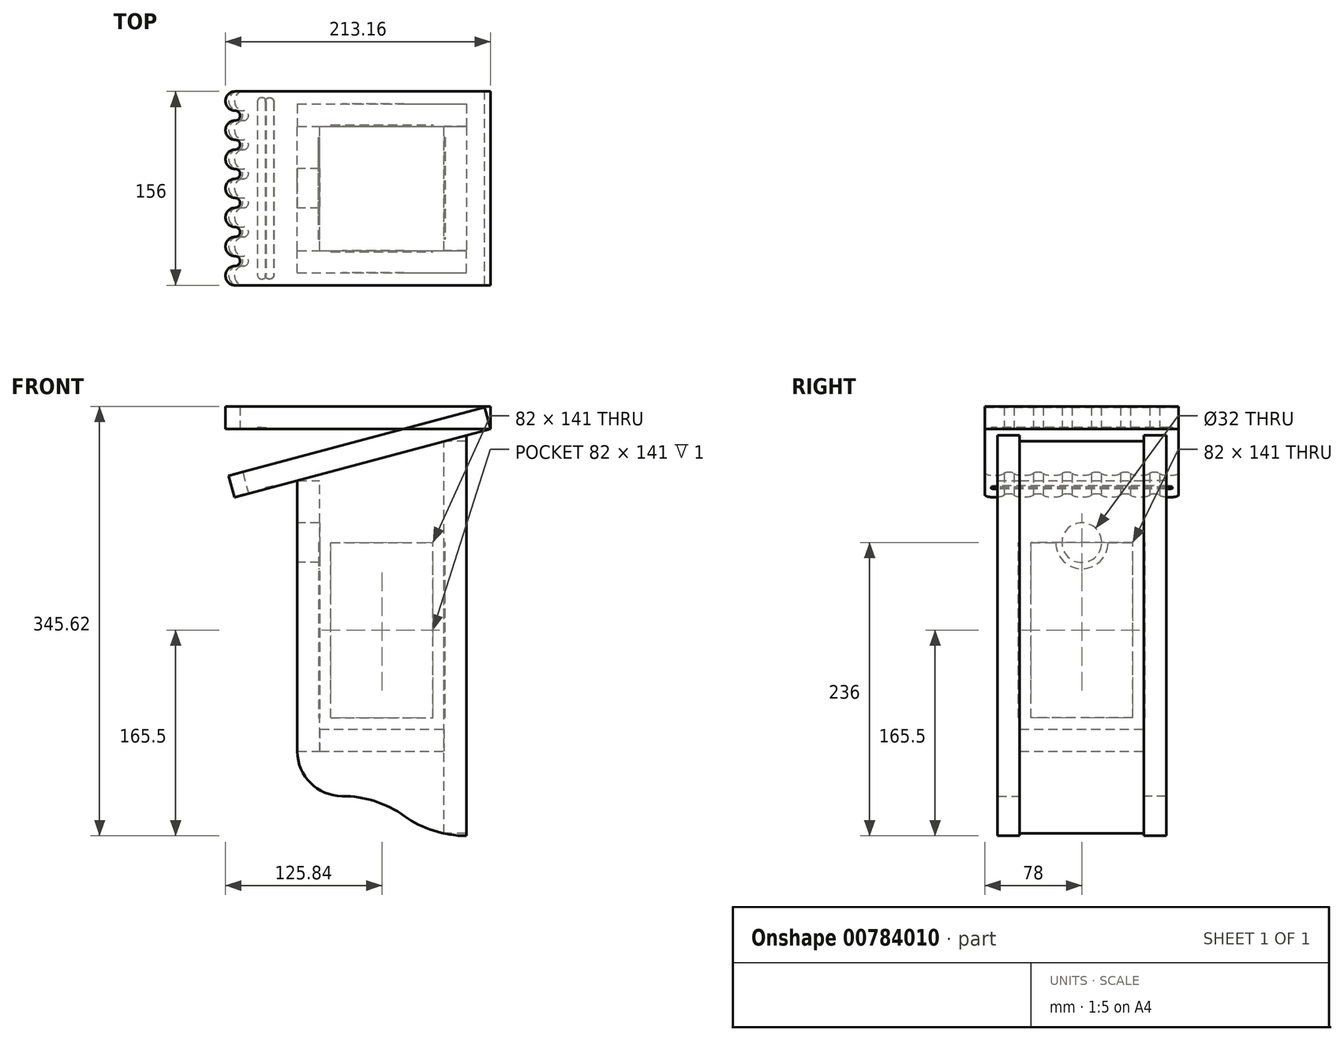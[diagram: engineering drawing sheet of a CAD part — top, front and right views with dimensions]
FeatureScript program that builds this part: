
annotation { "Feature Type Name" : "Feature", "Feature Type Description" : "" }
export const myFeature = defineFeature(function(context is Context, id is Id, definition is map)
    precondition{}
    {
        {
            assignVariable(context, id + "F0", {"name" : "Larg", "anyValue" : 100});
        }
        {
            assignVariable(context, id + "F1", {"name" : "Ep", "anyValue" : 18});
        }
        {
            var Q0;
            Q0=qCreatedBy(makeId("Front.planeOp"),FACE);
            cPlane(context, id + "F2", {"entities" : qUnion([Q0]), "cplaneType" : CPlaneType.OFFSET, "offset" : (getVariable(context, 'Larg') / 2) * mm, "width" : 150 * mm, "height" : 150 * mm});
        }
        {
            var Q0;
            Q0=qCreatedBy(id+"F2.planeOp",FACE);
            var sketch = newSketch(context, id + "F3", { "sketchPlane" : qUnion([Q0])});
            skLineSegment(sketch, "E0", {"start": v(-68, -109) * mm, "end": v(-68, 109) * mm});
            skLineSegment(sketch, "E1", {"start": v(-68, 109) * mm, "end": v(68, 145.44) * mm});
            skLineSegment(sketch, "E2", {"start": v(68, 145.44) * mm, "end": v(68, -109) * mm});
            skLineSegment(sketch, "E3", {"start": v(68, -109) * mm, "end": v(-68, -109) * mm});
            skLineSegment(sketch, "E4", {"start": v(68, -109) * mm, "end": v(68, -177) * mm});
            skArc(sketch, "E5", {"start": v(-68, -109) * mm, "mid": v(-57.46, -134.46) * mm, "end": v(-32, -145) * mm});
            skArc(sketch, "E6", {"start": v(-32, -145) * mm, "mid": v(-5.75, -149.1) * mm, "end": v(18, -161) * mm});
            skArc(sketch, "E7", {"start": v(68, -177) * mm, "mid": v(41.75, -172.9) * mm, "end": v(18, -161) * mm});
            skSolve(sketch);
        }
        {
            var Q0;
            Q0=qSketchRegion(id+"F3",true);
            extrude(context, id + "F4", {"entities" : qUnion([Q0]), "depth" : (getVariable(context, 'Ep')) * mm, "offsetDistance" : 25 * mm});
        }
        {
            var Q0;
            Q0=makeQuery(id+"F4.opExtrude","CAP_FACE",FACE,{"disambiguationData":[OSD([sQuery(id+"F3.wireOp",EDGE,"E0"),sQuery(id+"F3.wireOp",EDGE,"E1"),sQuery(id+"F3.wireOp",EDGE,"E2"),sQuery(id+"F3.wireOp",EDGE,"E4"),sQuery(id+"F3.wireOp",EDGE,"E5"),sQuery(id+"F3.wireOp",EDGE,"E6"),sQuery(id+"F3.wireOp",EDGE,"E7")])],"isStart":true});
            var sketch = newSketch(context, id + "F5", { "sketchPlane" : qUnion([Q0])});
            skLineSegment(sketch, "E8.bottom", {"start": v(41, -82) * mm, "end": v(-41, -82) * mm});
            skLineSegment(sketch, "E8.top", {"start": v(41, 59) * mm, "end": v(-41, 59) * mm});
            skLineSegment(sketch, "E8.left", {"start": v(41, -82) * mm, "end": v(41, 59) * mm});
            skLineSegment(sketch, "E8.right", {"start": v(-41, -82) * mm, "end": v(-41, 59) * mm});
            skSolve(sketch);
        }
        {
            var Q0;
            Q0 = qSketchRegion(id + "F5", true);
            extrude(context, id + "F6", {"entities" : qUnion([Q0]), "operationType" : NewBodyOperationType.REMOVE, "oppositeDirection" : true, "depth" : 1 * mm, "offsetDistance" : 25 * mm});
        }
        {
            var Q0;
            Q0=makeQuery(id+"F4.opExtrude","SWEPT_BODY",BODY,{"disambiguationData":[OSD([sQuery(id+"F3.wireOp",EDGE,"z3EwWfGW-5xOQ-D7vt-vxF3-r7Dkdny4VjHE"),sQuery(id+"F3.wireOp",EDGE,"Gt7UUSWQ-Rokf-2xSb-CDKS-a55I8TqbTzyF"),sQuery(id+"F3.wireOp",EDGE,"E0"),sQuery(id+"F3.wireOp",EDGE,"E1"),sQuery(id+"F3.wireOp",EDGE,"E2"),sQuery(id+"F3.wireOp",EDGE,"E3")])]});
            var Q1;
            Q1=qCreatedBy(makeId("Front.planeOp"),FACE);
            mirror(context, id + "F7", {"entities" : qUnion([Q0]), "mirrorPlane" : qUnion([Q1])});
        }
        {
            var Q0;
            Q0=makeQuery(id+"F7.opPattern","COPY",FACE,{"derivedFrom":makeQuery(id+"F4.opExtrude","CAP_FACE",FACE,{"disambiguationData":[OSD([sQuery(id+"F3.wireOp",EDGE,"z3EwWfGW-5xOQ-D7vt-vxF3-r7Dkdny4VjHE"),sQuery(id+"F3.wireOp",EDGE,"Gt7UUSWQ-Rokf-2xSb-CDKS-a55I8TqbTzyF"),sQuery(id+"F3.wireOp",EDGE,"E0"),sQuery(id+"F3.wireOp",EDGE,"E1"),sQuery(id+"F3.wireOp",EDGE,"E2"),sQuery(id+"F3.wireOp",EDGE,"E3")])],"isStart":true}),"instanceName":"1"});
            var sketch = newSketch(context, id + "F8", { "sketchPlane" : qUnion([Q0])});
            skLineSegment(sketch, "E9.bottom", {"start": v(-68, -109) * mm, "end": v(-50, -109) * mm});
            skLineSegment(sketch, "E9.top", {"start": v(-68, 109) * mm, "end": v(-50, 109) * mm});
            skLineSegment(sketch, "E9.left", {"start": v(-68, -109) * mm, "end": v(-68, 109) * mm});
            skLineSegment(sketch, "E9.right", {"start": v(-50, -109) * mm, "end": v(-50, 109) * mm});
            skSolve(sketch);
        }
        {
            var Q0;
            Q0=qSketchRegion(id+"F8",true);
            var Q1;
            Q1=makeQuery(id+"F4.opExtrude","CAP_FACE",FACE,{"disambiguationData":[OSD([sQuery(id+"F3.wireOp",EDGE,"z3EwWfGW-5xOQ-D7vt-vxF3-r7Dkdny4VjHE"),sQuery(id+"F3.wireOp",EDGE,"Gt7UUSWQ-Rokf-2xSb-CDKS-a55I8TqbTzyF"),sQuery(id+"F3.wireOp",EDGE,"E0"),sQuery(id+"F3.wireOp",EDGE,"E1"),sQuery(id+"F3.wireOp",EDGE,"E2"),sQuery(id+"F3.wireOp",EDGE,"E3")])],"isStart":true});
            extrude(context, id + "F9", {"entities" : qUnion([Q0]), "endBound" : BoundingType.UP_TO_SURFACE, "depth" : 25 * mm, "endBoundEntityFace" : qUnion([Q1]), "offsetDistance" : 25 * mm});
        }
        {
            var Q0;
            Q0=makeQuery(id+"F4.opExtrude","CAP_FACE",FACE,{"disambiguationData":[OSD([sQuery(id+"F3.wireOp",EDGE,"E0"),sQuery(id+"F3.wireOp",EDGE,"E1"),sQuery(id+"F3.wireOp",EDGE,"E2"),sQuery(id+"F3.wireOp",EDGE,"E4"),sQuery(id+"F3.wireOp",EDGE,"E5"),sQuery(id+"F3.wireOp",EDGE,"E6"),sQuery(id+"F3.wireOp",EDGE,"E7")])],"isStart":true});
            var sketch = newSketch(context, id + "F10", { "sketchPlane" : qUnion([Q0])});
            skLineSegment(sketch, "E10.bottom", {"start": v(-68, -175.1) * mm, "end": v(-50, -175.1) * mm});
            skLineSegment(sketch, "E10.top", {"start": v(-68, 140.62) * mm, "end": v(-50, 140.62) * mm});
            skLineSegment(sketch, "E10.left", {"start": v(-68, -175.1) * mm, "end": v(-68, 140.62) * mm});
            skLineSegment(sketch, "E10.right", {"start": v(-50, -175.1) * mm, "end": v(-50, 140.62) * mm});
            skSolve(sketch);
        }
        {
            var Q0;
            Q0=qSketchRegion(id+"F10",true);
            var Q1;
            Q1=makeQuery(id+"F7.opPattern","COPY",FACE,{"derivedFrom":makeQuery(id+"F4.opExtrude","CAP_FACE",FACE,{"disambiguationData":[OSD([sQuery(id+"F3.wireOp",EDGE,"E0"),sQuery(id+"F3.wireOp",EDGE,"E1"),sQuery(id+"F3.wireOp",EDGE,"E2"),sQuery(id+"F3.wireOp",EDGE,"E4"),sQuery(id+"F3.wireOp",EDGE,"E5"),sQuery(id+"F3.wireOp",EDGE,"E6"),sQuery(id+"F3.wireOp",EDGE,"E7")])],"isStart":true}),"instanceName":"1"});
            extrude(context, id + "F11", {"entities" : qUnion([Q0]), "endBound" : BoundingType.UP_TO_SURFACE, "depth" : (getVariable(context, 'Ep')) * mm, "endBoundEntityFace" : qUnion([Q1]), "offsetDistance" : 25 * mm});
        }
        {
            var Q0;
            Q0=makeQuery(id+"F11.opExtrude","SWEPT_FACE",FACE,{"disambiguationData":[OSD([sQuery(id+"F10.wireOp",EDGE,"E10.right")])]});
            var sketch = newSketch(context, id + "F12", { "sketchPlane" : qUnion([Q0])});
            skLineSegment(sketch, "E11.bottom", {"start": v(-41, -82) * mm, "end": v(41, -82) * mm});
            skLineSegment(sketch, "E11.top", {"start": v(-41, 59) * mm, "end": v(41, 59) * mm});
            skLineSegment(sketch, "E11.left", {"start": v(-41, -82) * mm, "end": v(-41, 59) * mm});
            skLineSegment(sketch, "E11.right", {"start": v(41, -82) * mm, "end": v(41, 59) * mm});
            skSolve(sketch);
        }
        {
            var Q0;
            Q0=makeQuery(id+"F4.opExtrude","SWEPT_FACE",FACE,{"disambiguationData":[OSD([sQuery(id+"F3.wireOp",EDGE,"E1")])]});
            var sketch = newSketch(context, id + "F13", { "sketchPlane" : qUnion([Q0])});
            skLineSegment(sketch, "E12.bottom", {"start": v(123.33, -78) * mm, "end": v(-82.09, -78) * mm});
            skLineSegment(sketch, "E12.top", {"start": v(123.33, 78) * mm, "end": v(-82.09, 78) * mm});
            skLineSegment(sketch, "E12.left", {"start": v(-82.09, -78) * mm, "end": v(-82.09, 78) * mm, "construction": true});
            skLineSegment(sketch, "E12.right", {"start": v(123.33, -78) * mm, "end": v(123.33, 78) * mm});
            skArc(sketch, "E13", {"start": v(-82.09, 62.5) * mm, "mid": v(-89.84, 70.25) * mm, "end": v(-82.09, 78) * mm});
            skArc(sketch, "E14", {"start": v(-82.09, 54.58) * mm, "mid": v(-89.84, 46.83) * mm, "end": v(-82.09, 39.08) * mm});
            skArc(sketch, "E15", {"start": v(-82.09, 31.17) * mm, "mid": v(-89.84, 23.42) * mm, "end": v(-82.09, 15.67) * mm});
            skArc(sketch, "E16", {"start": v(-82.09, 62.5) * mm, "mid": v(-78.13, 58.54) * mm, "end": v(-82.09, 54.58) * mm});
            skArc(sketch, "E17", {"start": v(-82.09, 39.08) * mm, "mid": v(-78.13, 35.12) * mm, "end": v(-82.09, 31.17) * mm});
            skArc(sketch, "E18", {"start": v(-82.09, 15.67) * mm, "mid": v(-78.13, 11.7) * mm, "end": v(-82.09, 7.75) * mm});
            skArc(sketch, "E19", {"start": v(-82.09, 7.75) * mm, "mid": v(-89.84, 0) * mm, "end": v(-82.09, -7.75) * mm});
            skArc(sketch, "E20", {"start": v(-82.09, -7.75) * mm, "mid": v(-78.13, -11.7) * mm, "end": v(-82.09, -15.67) * mm});
            skArc(sketch, "E21", {"start": v(-82.09, -15.67) * mm, "mid": v(-89.84, -23.42) * mm, "end": v(-82.09, -31.17) * mm});
            skArc(sketch, "E22", {"start": v(-82.09, -31.17) * mm, "mid": v(-78.13, -35.13) * mm, "end": v(-82.09, -39.08) * mm});
            skArc(sketch, "E23", {"start": v(-82.09, -39.08) * mm, "mid": v(-89.84, -46.83) * mm, "end": v(-82.09, -54.58) * mm});
            skArc(sketch, "E24", {"start": v(-82.09, -54.58) * mm, "mid": v(-78.13, -58.54) * mm, "end": v(-82.09, -62.5) * mm});
            skArc(sketch, "E25", {"start": v(-82.09, -62.5) * mm, "mid": v(-89.84, -70.25) * mm, "end": v(-82.09, -78) * mm});
            skSolve(sketch);
        }
        {
            var Q0;
            Q0=qSketchRegion(id+"F13",true);
            extrude(context, id + "F14", {"entities" : qUnion([Q0]), "depth" : (getVariable(context, 'Ep')) * mm, "offsetDistance" : 25 * mm});
        }
        {
            var Q0;
            Q0=makeQuery(id+"F9.opExtrude","SWEPT_FACE",FACE,{"disambiguationData":[OSD([sQuery(id+"F8.wireOp",EDGE,"E9.left")])]});
            var sketch = newSketch(context, id + "F15", { "sketchPlane" : qUnion([Q0])});
            skCircle(sketch, "E26", {"center": v(0, 59) * mm, "radius": 16 * mm});
            skSolve(sketch);
        }
        {
            var Q0;
            Q0=qSketchRegion(id+"F15",true);
            var Q1;
            Q1=makeQuery(id+"F9.opExtrude","SWEPT_FACE",FACE,{"disambiguationData":[OSD([sQuery(id+"F8.wireOp",EDGE,"E9.right")])]});
            extrude(context, id + "F16", {"entities" : qUnion([Q0]), "operationType" : NewBodyOperationType.REMOVE, "endBound" : BoundingType.UP_TO_SURFACE, "oppositeDirection" : true, "depth" : 25 * mm, "endBoundEntityFace" : qUnion([Q1]), "offsetDistance" : 25 * mm});
        }
        {
            var Q0;
            Q0=makeQuery(id+"F9.opExtrude","SWEPT_FACE",FACE,{"disambiguationData":[OSD([sQuery(id+"F8.wireOp",EDGE,"E9.bottom")])]});
            var sketch = newSketch(context, id + "F17", { "sketchPlane" : qUnion([Q0])});
            skLineSegment(sketch, "E27.bottom", {"start": v(-50, 50) * mm, "end": v(50, 50) * mm});
            skLineSegment(sketch, "E27.top", {"start": v(-50, -50) * mm, "end": v(50, -50) * mm});
            skLineSegment(sketch, "E27.left", {"start": v(-50, 50) * mm, "end": v(-50, -50) * mm});
            skLineSegment(sketch, "E27.right", {"start": v(50, 50) * mm, "end": v(50, -50) * mm});
            skSolve(sketch);
        }
        {
            var Q0;
            Q0 = qSketchRegion(id + "F17", true);
            extrude(context, id + "F18", {"entities" : qUnion([Q0]), "oppositeDirection" : true, "depth" : (getVariable(context, 'Ep')) * mm, "offsetDistance" : 25 * mm});
        }
        {
            var Q0;
            Q0=makeQuery(id+"F9.opExtrude","SWEPT_FACE",FACE,{"disambiguationData":[OSD([sQuery(id+"F8.wireOp",EDGE,"E9.right")])]});
            var sketch = newSketch(context, id + "F19", { "sketchPlane" : qUnion([Q0])});
            skLineSegment(sketch, "E28.bottom", {"start": v(-41, 59) * mm, "end": v(-21, 59) * mm});
            skLineSegment(sketch, "E28.top", {"start": v(-41, -82) * mm, "end": v(41, -82) * mm});
            skLineSegment(sketch, "E28.left", {"start": v(-41, 59) * mm, "end": v(-41, -82) * mm});
            skLineSegment(sketch, "E28.right", {"start": v(41, 59) * mm, "end": v(41, -82) * mm});
            skArc(sketch, "E29", {"start": v(21, 59) * mm, "mid": v(0, 38) * mm, "end": v(-21, 59) * mm});
            skLineSegment(sketch, "E30.trimOffspring", {"start": v(21, 59) * mm, "end": v(41, 59) * mm});
            skSolve(sketch);
        }
        {
            var Q0;
            Q0 = qSketchRegion(id + "F19", true);
            extrude(context, id + "F20", {"entities" : qUnion([Q0]), "operationType" : NewBodyOperationType.REMOVE, "oppositeDirection" : true, "depth" : 1 * mm, "offsetDistance" : 25 * mm});
        }
        {
            var Q0;
            Q0=makeQuery(id+"F14.opExtrude","CAP_FACE",FACE,{"disambiguationData":[OSD([sQuery(id+"F13.wireOp",EDGE,"E12.bottom"),sQuery(id+"F13.wireOp",EDGE,"E12.top"),sQuery(id+"F13.wireOp",EDGE,"E12.right"),sQuery(id+"F13.wireOp",EDGE,"E13"),sQuery(id+"F13.wireOp",EDGE,"E14"),sQuery(id+"F13.wireOp",EDGE,"E15"),sQuery(id+"F13.wireOp",EDGE,"E16"),sQuery(id+"F13.wireOp",EDGE,"E17"),sQuery(id+"F13.wireOp",EDGE,"E18"),sQuery(id+"F13.wireOp",EDGE,"E19"),sQuery(id+"F13.wireOp",EDGE,"E20"),sQuery(id+"F13.wireOp",EDGE,"E21"),sQuery(id+"F13.wireOp",EDGE,"E22"),sQuery(id+"F13.wireOp",EDGE,"E23"),sQuery(id+"F13.wireOp",EDGE,"E24"),sQuery(id+"F13.wireOp",EDGE,"E25")])],"isStart":true});
            var sketch = newSketch(context, id + "F21", { "sketchPlane" : qUnion([Q0])});
            skLineSegment(sketch, "E31.left", {"start": v(-64.09, -69.8) * mm, "end": v(-64.09, 69.8) * mm});
            skLineSegment(sketch, "E31.right", {"start": v(-57.09, -69.8) * mm, "end": v(-57.09, 69.8) * mm});
            skLineSegment(sketch, "E32", {"start": v(-60.89, -73) * mm, "end": v(-60.29, -73) * mm});
            skLineSegment(sketch, "E33", {"start": v(-60.89, 73) * mm, "end": v(-60.29, 73) * mm});
            skPoint(sketch, "E34.visualSharp", {"position": v(-57.09, -73) * mm});
            skArc(sketch, "E34.filletArc", {"start": v(-60.29, -73) * mm, "mid": v(-58.02, -72.06) * mm, "end": v(-57.09, -69.8) * mm});
            skPoint(sketch, "E35.visualSharp", {"position": v(-64.09, -73) * mm});
            skArc(sketch, "E35.filletArc", {"start": v(-64.09, -69.8) * mm, "mid": v(-63.15, -72.06) * mm, "end": v(-60.89, -73) * mm});
            skPoint(sketch, "E36.visualSharp", {"position": v(-57.09, 73) * mm});
            skArc(sketch, "E36.filletArc", {"start": v(-57.09, 69.8) * mm, "mid": v(-58.02, 72.06) * mm, "end": v(-60.29, 73) * mm});
            skPoint(sketch, "E37.visualSharp", {"position": v(-64.09, 73) * mm});
            skArc(sketch, "E37.filletArc", {"start": v(-60.89, 73) * mm, "mid": v(-63.15, 72.06) * mm, "end": v(-64.09, 69.8) * mm});
            skSolve(sketch);
        }
        {
            var Q0;
            Q0 = qSketchRegion(id + "F21", true);
            extrude(context, id + "F22", {"entities" : qUnion([Q0]), "operationType" : NewBodyOperationType.REMOVE, "oppositeDirection" : true, "depth" : 1 * mm, "offsetDistance" : 25 * mm});
        }
        {
            var Q0;
            Q0=makeQuery(id+"F14.opExtrude","SWEPT_BODY",BODY,{"disambiguationData":[OSD([sQuery(id+"F13.wireOp",EDGE,"E12.bottom"),sQuery(id+"F13.wireOp",EDGE,"E12.top"),sQuery(id+"F13.wireOp",EDGE,"E12.right"),sQuery(id+"F13.wireOp",EDGE,"E13"),sQuery(id+"F13.wireOp",EDGE,"E14"),sQuery(id+"F13.wireOp",EDGE,"E15"),sQuery(id+"F13.wireOp",EDGE,"E16"),sQuery(id+"F13.wireOp",EDGE,"E17"),sQuery(id+"F13.wireOp",EDGE,"E18"),sQuery(id+"F13.wireOp",EDGE,"E19"),sQuery(id+"F13.wireOp",EDGE,"E20"),sQuery(id+"F13.wireOp",EDGE,"E21"),sQuery(id+"F13.wireOp",EDGE,"E22"),sQuery(id+"F13.wireOp",EDGE,"E23"),sQuery(id+"F13.wireOp",EDGE,"E24"),sQuery(id+"F13.wireOp",EDGE,"E25")])]});
            var Q1;
            Q1=makeQuery(id+"F14.opExtrude","CAP_EDGE",EDGE,{"disambiguationData":[OSD([sQuery(id+"F13.wireOp",EDGE,"E12.right")])],"isStart":true});
            transform(context, id + "F23", {"entities" : qUnion([Q0]), "transformType" : TransformType.ROTATION, "transformAxis" : qUnion([Q1]), "angle" : 15 * degree, "makeCopy" : true});
        }
        {
            var Q0;
            Q0 = qSketchRegion(id + "F12", true);
            extrude(context, id + "F24", {"entities" : qUnion([Q0]), "operationType" : NewBodyOperationType.REMOVE, "oppositeDirection" : true, "depth" : 1 * mm, "offsetDistance" : 25 * mm});
        }
    });
